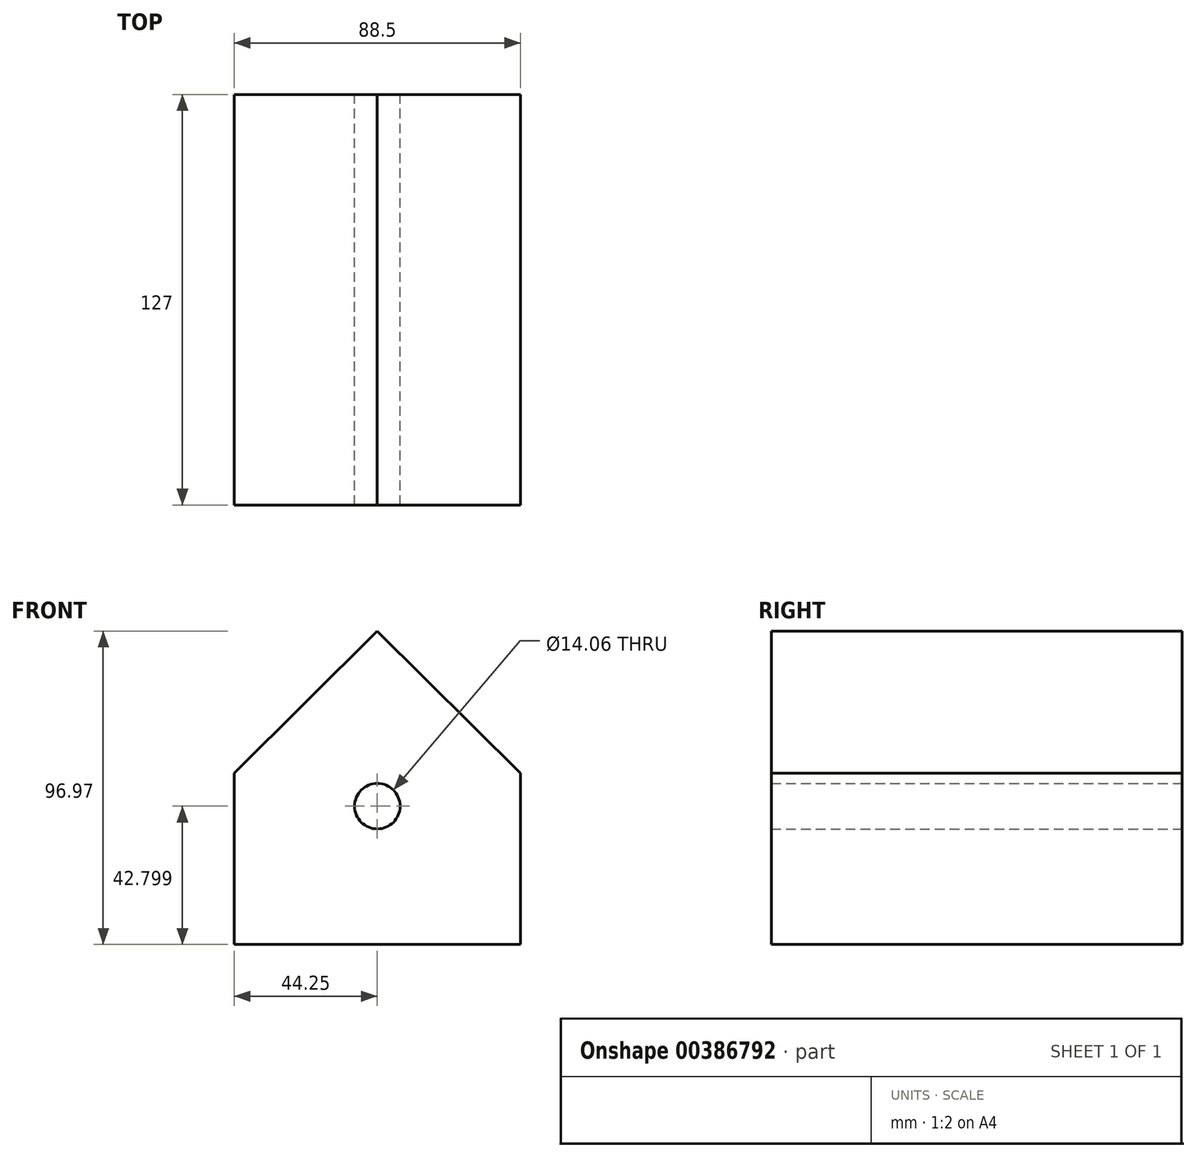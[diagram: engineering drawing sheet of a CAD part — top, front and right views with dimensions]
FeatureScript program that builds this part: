
annotation { "Feature Type Name" : "Feature", "Feature Type Description" : "" }
export const myFeature = defineFeature(function(context is Context, id is Id, definition is map)
    precondition{}
    {
        {
            var Q0;
            Q0=qCreatedBy(makeId("Front.planeOp"),FACE);
            var sketch = newSketch(context, id + "F0", { "sketchPlane" : qUnion([Q0])});
            skLineSegment(sketch, "E0.bottom", {"start": v(44.25, -26.5) * mm, "end": v(-44.25, -26.5) * mm});
            skLineSegment(sketch, "E0.top", {"start": v(44.25, 26.5) * mm, "end": v(-44.25, 26.5) * mm});
            skLineSegment(sketch, "E0.left", {"start": v(44.25, -26.5) * mm, "end": v(44.25, 26.5) * mm});
            skLineSegment(sketch, "E0.right", {"start": v(-44.25, -26.5) * mm, "end": v(-44.25, 26.5) * mm});
            skPoint(sketch, "E0.middle", {"position": v(0, 0) * mm});
            skLineSegment(sketch, "E1", {"start": v(-44.25, 26.5) * mm, "end": v(0, 70.47) * mm});
            skLineSegment(sketch, "E2", {"start": v(0, 70.47) * mm, "end": v(44.25, 26.5) * mm});
            skCircle(sketch, "E3", {"center": v(0, 16.3) * mm, "radius": 7.03 * mm});
            skSolve(sketch);
        }
        {
            var Q0;
            Q0 = qSketchRegion(id + "F0", true);
            extrude(context, id + "F1", {"entities" : qUnion([Q0]), "depth" : 127 * mm});
        }
    });
